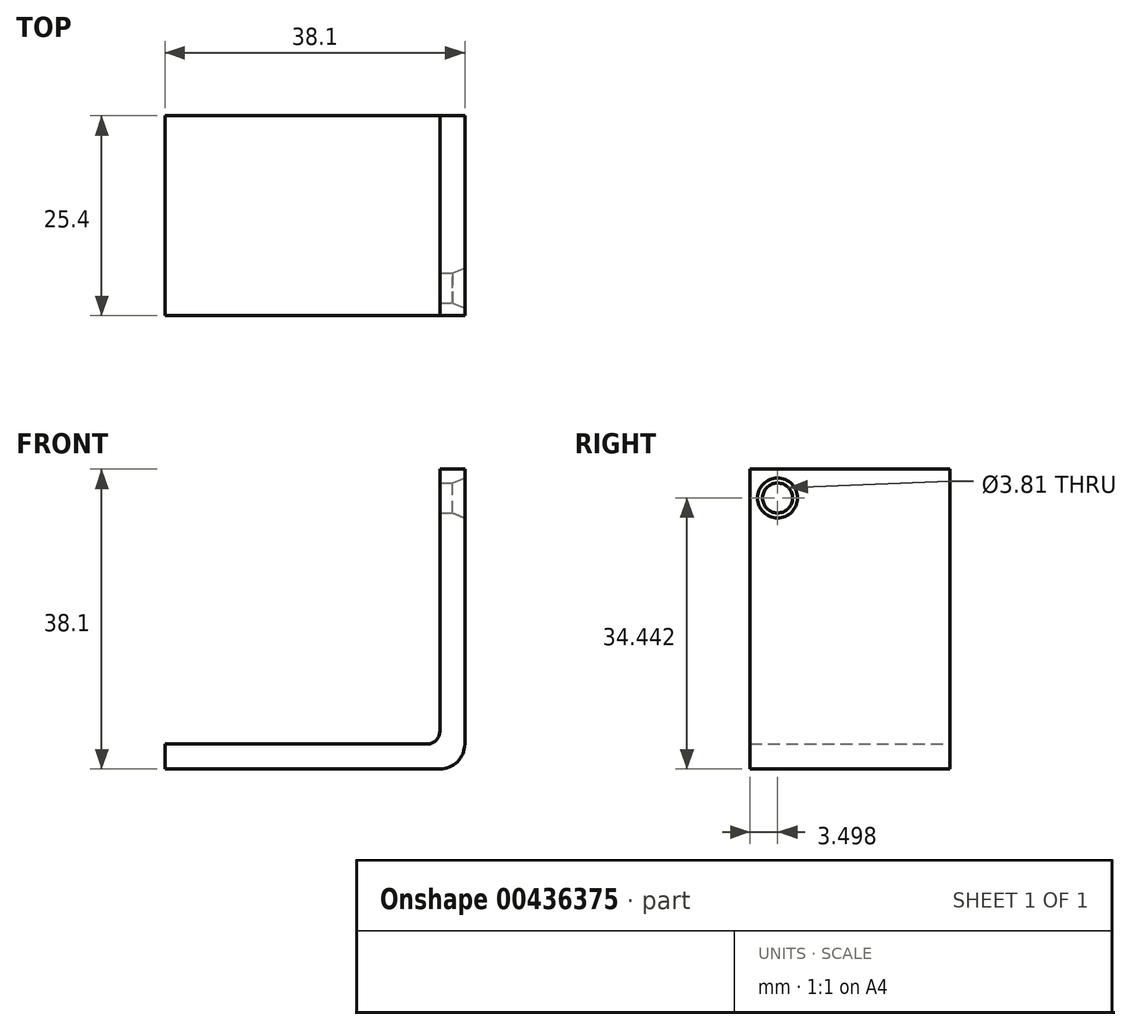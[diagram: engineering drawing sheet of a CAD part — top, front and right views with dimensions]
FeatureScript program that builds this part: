
annotation { "Feature Type Name" : "Feature", "Feature Type Description" : "" }
export const myFeature = defineFeature(function(context is Context, id is Id, definition is map)
    precondition{}
    {
        {
            var Q0;
            Q0=qCreatedBy(makeId("Front.planeOp"),FACE);
            var sketch = newSketch(context, id + "F0", { "sketchPlane" : qUnion([Q0])});
            skLineSegment(sketch, "E0.bottom", {"start": v(-3.18, 4.76) * mm, "end": v(-38.1, 4.76) * mm});
            skLineSegment(sketch, "E0.top", {"start": v(-4.76, 7.94) * mm, "end": v(-38.1, 7.94) * mm});
            skLineSegment(sketch, "E0.left", {"start": v(0, 3.18) * mm, "end": v(0, 4.76) * mm});
            skLineSegment(sketch, "E0.right", {"start": v(-38.1, 4.76) * mm, "end": v(-38.1, 7.94) * mm});
            skLineSegment(sketch, "E1.top", {"start": v(0, 42.86) * mm, "end": v(-3.18, 42.86) * mm});
            skLineSegment(sketch, "E1.left", {"start": v(0, 7.94) * mm, "end": v(0, 42.86) * mm});
            skLineSegment(sketch, "E1.right", {"start": v(-3.18, 9.53) * mm, "end": v(-3.18, 42.86) * mm});
            skPoint(sketch, "E2.visualSharp", {"position": v(-3.18, 7.94) * mm});
            skArc(sketch, "E2.filletArc", {"start": v(-4.76, 7.94) * mm, "mid": v(-3.64, 8.4) * mm, "end": v(-3.18, 9.53) * mm});
            skPoint(sketch, "E3.newPointA", {"position": v(0, 4.76) * mm});
            skPoint(sketch, "E3.newPointB", {"position": v(0, 4.76) * mm});
            skArc(sketch, "E3.filletArc", {"start": v(-3.18, 4.76) * mm, "mid": v(-0.93, 5.7) * mm, "end": v(0, 7.94) * mm});
            skSolve(sketch);
        }
        {
            var Q0;
            Q0=makeQuery(id+"F0.imprint","IMPRINT",FACE,{"disambiguationData":[TD([[makeQuery(id+"F0.imprint","IMPRINT",EDGE,{"derivedFrom":sQuery(id+"F0.wireOp",EDGE,"E0.bottom")}),-1.0]])]});
            extrude(context, id + "F1", {"entities" : qUnion([Q0]), "endBound" : BoundingType.SYMMETRIC, "depth" : 25.4 * mm});
        }
        {
            var Q0;
            Q0=makeQuery(id+"F1.opExtrude","SWEPT_FACE",FACE,{"disambiguationData":[OSD([sQuery(id+"F0.wireOp",EDGE,"E1.left")])]});
            var sketch = newSketch(context, id + "F2", { "sketchPlane" : qUnion([Q0])});
            skCircle(sketch, "E4", {"center": v(-9.2, 39.2) * mm, "radius": 1.03 * mm});
            skSolve(sketch);
        }
        {
            var Q0;
            Q0=sQuery(id+"F2.wireOp",VERTEX,"E4.center");
            var Q1;
            Q1=makeQuery(id+"F1.opExtrude","SWEPT_BODY",BODY,{"disambiguationData":[OSD([sQuery(id+"F0.wireOp",EDGE,"E0.bottom"),sQuery(id+"F0.wireOp",EDGE,"E0.top"),sQuery(id+"F0.wireOp",EDGE,"E0.right"),sQuery(id+"F0.wireOp",EDGE,"E1.top"),sQuery(id+"F0.wireOp",EDGE,"E1.left"),sQuery(id+"F0.wireOp",EDGE,"E1.right"),sQuery(id+"F0.wireOp",EDGE,"E2.filletArc"),sQuery(id+"F0.wireOp",EDGE,"E3.filletArc")])]});
            hole(context, id + "F3", {"style" : HoleStyle.C_SINK, "endStyle" : HoleEndStyle.THROUGH, "holeDiameter" : 3.8 * mm, "cSinkDiameter" : 5.08 * mm, "cSinkAngle" : 45 * degree, "isTappedThrough" : true, "tappedDepth" : 12.7 * mm, "tapClearance" : 3, "locations" : qUnion([Q0]), "scope" : qUnion([Q1])});
        }
    });
